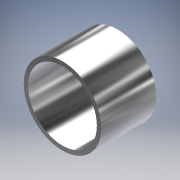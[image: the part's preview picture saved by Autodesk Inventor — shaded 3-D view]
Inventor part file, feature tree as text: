
AUTODESK INVENTOR PART (.ipt)
format: ipt  version: 2018 (Build 220112000, 112)  size: 125,952 bytes
history: native  units: in
note: dims shown in document units (in); Inventor stores cm internally (conversion verified against a paired STEP export)
features: extrude x1, sketch x1
ambient origin geometry x8: Origin, YZ Plane, XZ Plane, XY Plane, X Axis, Y Axis, Z Axis, Center Point
bodies: Solid1 (feature_tree)
feature tree (2):
  extrude  "Extrusion1"  Depth=2.55in TaperAngle=0.0deg
  sketch  "Sketch1"  dims[d1=0.25in d2=2.55in d3=0.0in d4=4.0in]
